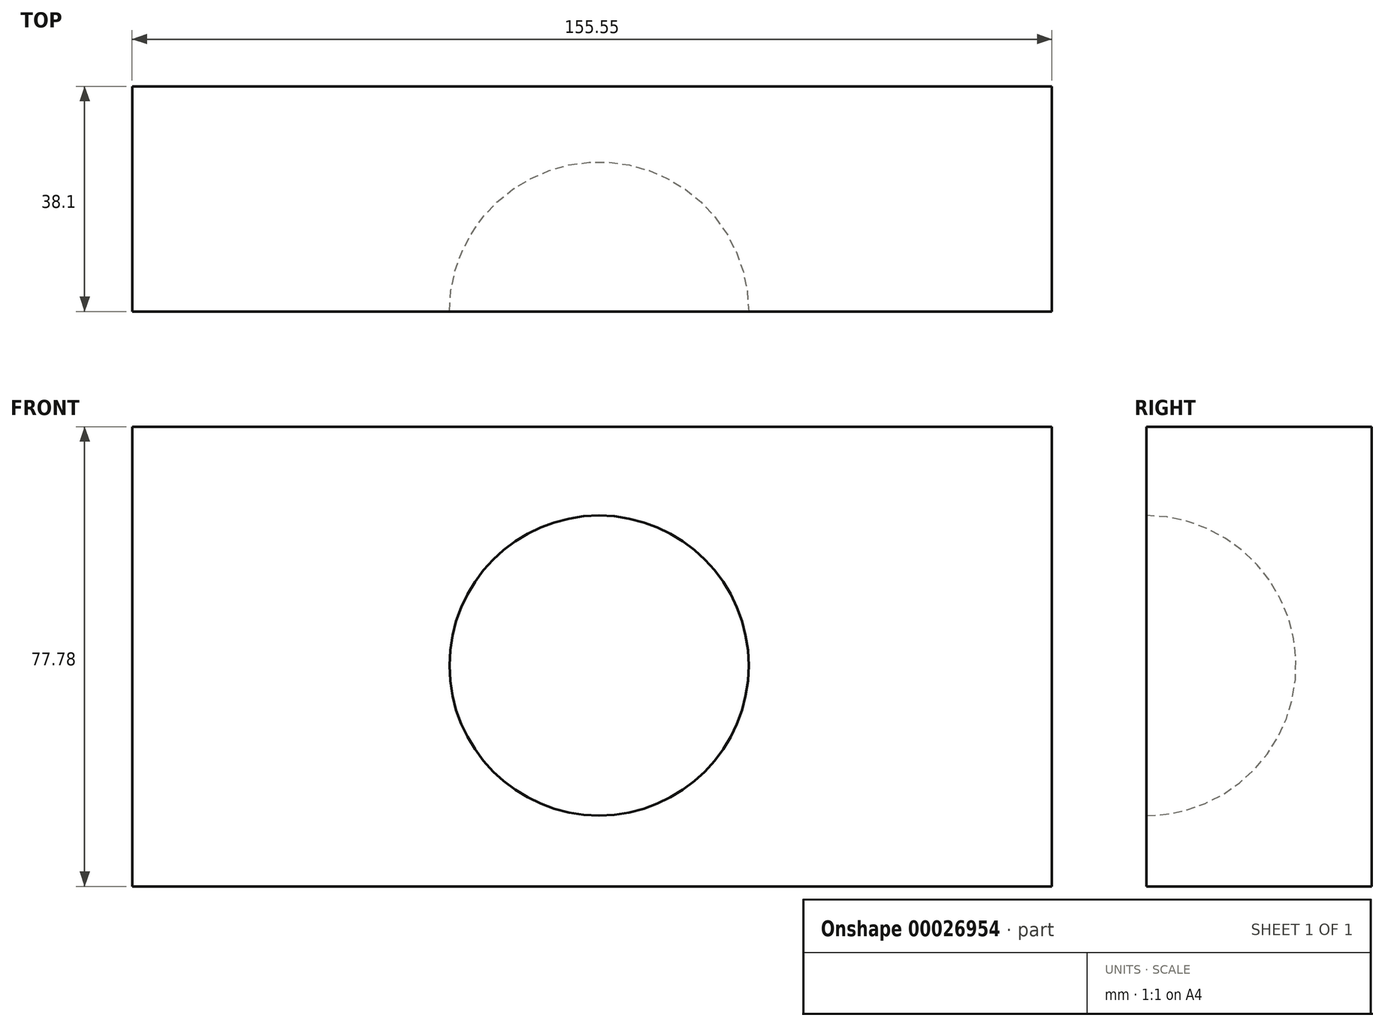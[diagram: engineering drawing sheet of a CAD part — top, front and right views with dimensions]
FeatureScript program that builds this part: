
annotation { "Feature Type Name" : "Feature", "Feature Type Description" : "" }
export const myFeature = defineFeature(function(context is Context, id is Id, definition is map)
    precondition{}
    {
        {
            var Q0;
            Q0=qCreatedBy(makeId("Front.planeOp"),FACE);
            var sketch = newSketch(context, id + "F0", { "sketchPlane" : qUnion([Q0])});
            skLineSegment(sketch, "E0.bottom", {"start": v(-78.97, 40.38) * mm, "end": v(76.58, 40.38) * mm});
            skLineSegment(sketch, "E0.top", {"start": v(-78.97, -37.4) * mm, "end": v(76.58, -37.4) * mm});
            skLineSegment(sketch, "E0.left", {"start": v(-78.97, 40.38) * mm, "end": v(-78.97, -37.4) * mm});
            skLineSegment(sketch, "E0.right", {"start": v(76.58, 40.38) * mm, "end": v(76.58, -37.4) * mm});
            skSolve(sketch);
        }
        {
            var Q0;
            Q0=makeQuery(id+"F0.imprint","IMPRINT",FACE,{"disambiguationData":[TD([[makeQuery(id+"F0.imprint","IMPRINT",EDGE,{"derivedFrom":sQuery(id+"F0.wireOp",EDGE,"E0.bottom")}),-1.0]])]});
            extrude(context, id + "F1", {"entities" : qUnion([Q0]), "depth" : 38.1 * mm});
        }
        {
            var Q0;
            Q0=makeQuery(id+"F1.opExtrude","CAP_FACE",FACE,{"disambiguationData":[OSD([sQuery(id+"F0.wireOp",EDGE,"E0.bottom"),sQuery(id+"F0.wireOp",EDGE,"E0.top"),sQuery(id+"F0.wireOp",EDGE,"E0.left"),sQuery(id+"F0.wireOp",EDGE,"E0.right")])],"isStart":false});
            var sketch = newSketch(context, id + "F2", { "sketchPlane" : qUnion([Q0])});
            skLineSegment(sketch, "E1", {"start": v(0, 25.36) * mm, "end": v(0, -25.44) * mm});
            skArc(sketch, "E2", {"start": v(0, -25.44) * mm, "mid": v(25.3, -0.04) * mm, "end": v(0, 25.36) * mm});
            skSolve(sketch);
        }
        {
            var Q0;
            Q0=makeQuery(id+"F2.imprint","IMPRINT",FACE,{"disambiguationData":[TD([[makeQuery(id+"F2.imprint","IMPRINT",EDGE,{"derivedFrom":sQuery(id+"F2.wireOp",EDGE,"E1")}),1.0]])]});
            var Q1;
            Q1=sQuery(id+"F2.wireOp",EDGE,"E1");
            revolve(context, id + "F3", {"operationType" : NewBodyOperationType.REMOVE, "entities" : qUnion([Q0]), "axis" : qUnion([Q1]), "revolveType" : RevolveType.FULL, "oppositeDirection" : true});
        }
    });
